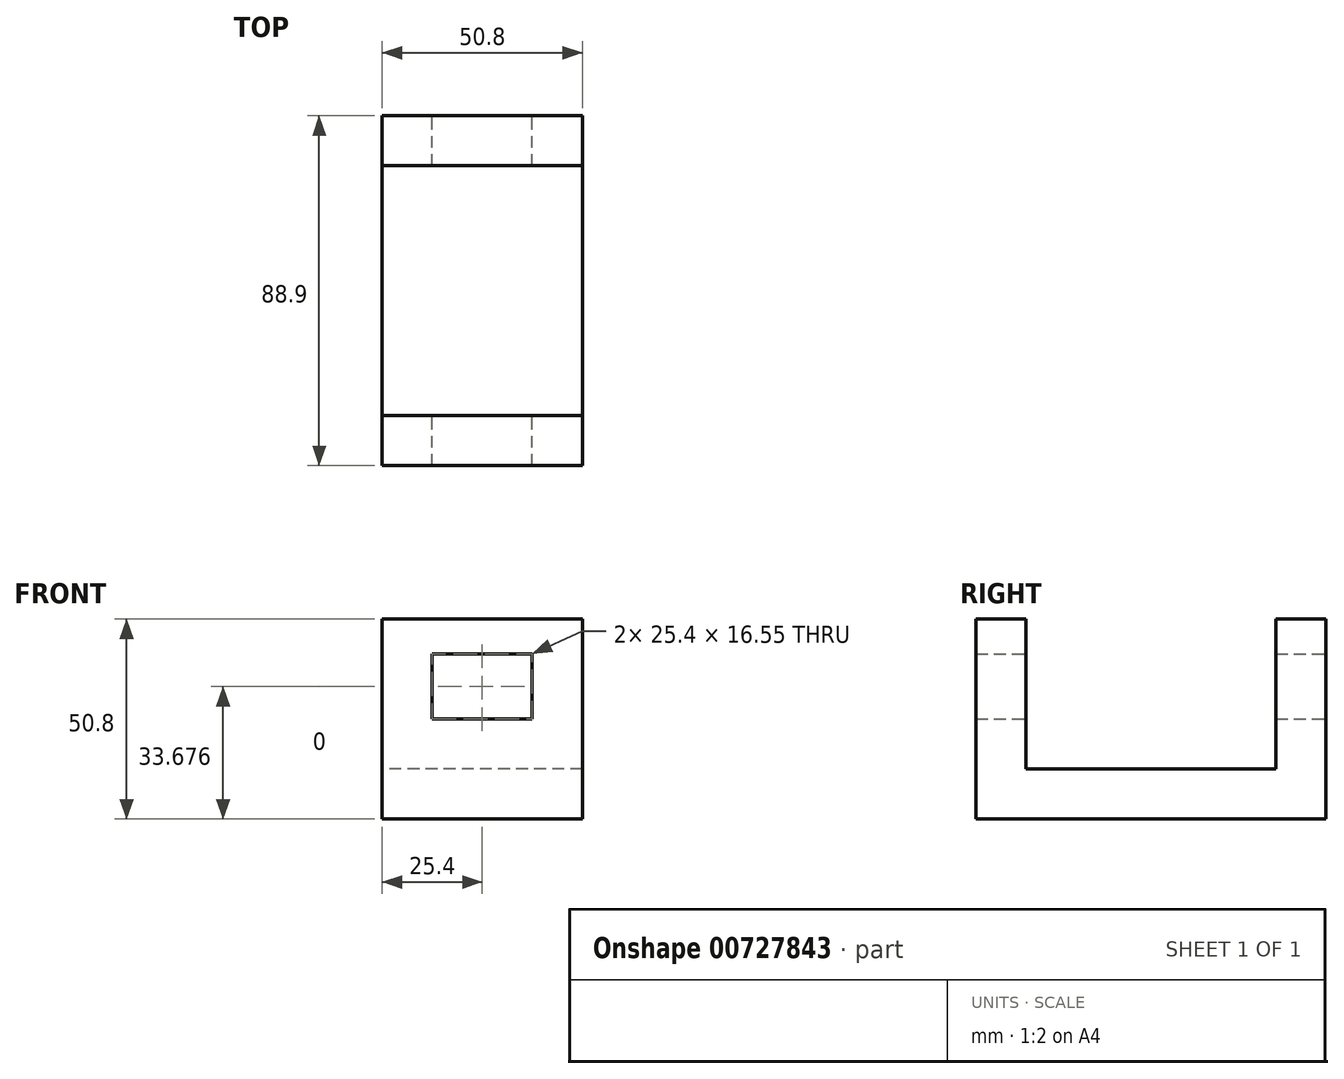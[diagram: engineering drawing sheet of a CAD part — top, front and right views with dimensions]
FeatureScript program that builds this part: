
annotation { "Feature Type Name" : "Feature", "Feature Type Description" : "" }
export const myFeature = defineFeature(function(context is Context, id is Id, definition is map)
    precondition{}
    {
        {
            var Q0;
            Q0=qCreatedBy(makeId("Right.planeOp"),FACE);
            var sketch = newSketch(context, id + "F0", { "sketchPlane" : qUnion([Q0])});
            skLineSegment(sketch, "E0.bottom", {"start": v(44.45, -6.35) * mm, "end": v(-44.45, -6.35) * mm});
            skLineSegment(sketch, "E0.top", {"start": v(44.45, 6.35) * mm, "end": v(-44.45, 6.35) * mm});
            skLineSegment(sketch, "E0.left", {"start": v(44.45, -6.35) * mm, "end": v(44.45, 6.35) * mm});
            skLineSegment(sketch, "E0.right", {"start": v(-44.45, -6.35) * mm, "end": v(-44.45, 6.35) * mm});
            skPoint(sketch, "E0.middle", {"position": v(0, 0) * mm});
            skLineSegment(sketch, "E1.bottom", {"start": v(-44.45, -6.35) * mm, "end": v(-31.75, -6.35) * mm});
            skLineSegment(sketch, "E1.top", {"start": v(-44.45, 44.45) * mm, "end": v(-31.75, 44.45) * mm});
            skLineSegment(sketch, "E1.left", {"start": v(-44.45, -6.35) * mm, "end": v(-44.45, 44.45) * mm});
            skLineSegment(sketch, "E1.right", {"start": v(-31.75, -6.35) * mm, "end": v(-31.75, 44.45) * mm});
            skPoint(sketch, "E2.oppositeSnap0", {"position": v(0, -6.35) * mm});
            skLineSegment(sketch, "E2.bottom", {"start": v(0, 49.89) * mm, "end": v(0, 49.89) * mm});
            skLineSegment(sketch, "E2.top", {"start": v(0, -32.21) * mm, "end": v(0, -32.21) * mm});
            skLineSegment(sketch, "E2.left", {"start": v(0, 49.89) * mm, "end": v(0, -32.21) * mm, "construction": true});
            skLineSegment(sketch, "E2.right", {"start": v(0, 49.89) * mm, "end": v(0, -32.21) * mm, "construction": true});
            skLineSegment(sketch, "E3.MirrorCS", {"start": v(44.45, -6.35) * mm, "end": v(44.45, 44.45) * mm});
            skLineSegment(sketch, "E4.MirrorCS", {"start": v(44.45, 44.45) * mm, "end": v(31.75, 44.45) * mm});
            skLineSegment(sketch, "E5.MirrorCS", {"start": v(31.75, -6.35) * mm, "end": v(31.75, 44.45) * mm});
            skSolve(sketch);
        }
        {
            var Q0;
            Q0 = qSketchRegion(id + "F0", true);
            extrude(context, id + "F1", {"entities" : qUnion([Q0]), "depth" : 50.8 * mm, "offsetDistance" : 25.4 * mm});
        }
        {
            var Q0;
            Q0=makeQuery(id+"F1.opExtrude","SWEPT_FACE",FACE,{"disambiguationData":[OSD([sQuery(id+"F0.wireOp",EDGE,"E3.MirrorCS")])]});
            var sketch = newSketch(context, id + "F2", { "sketchPlane" : qUnion([Q0])});
            skLineSegment(sketch, "E6.bottom", {"start": v(-38.1, 35.6) * mm, "end": v(-12.7, 35.6) * mm});
            skLineSegment(sketch, "E6.top", {"start": v(-38.1, 19.05) * mm, "end": v(-12.7, 19.05) * mm});
            skLineSegment(sketch, "E6.left", {"start": v(-38.1, 35.6) * mm, "end": v(-38.1, 19.05) * mm});
            skLineSegment(sketch, "E6.right", {"start": v(-12.7, 35.6) * mm, "end": v(-12.7, 19.05) * mm});
            skSolve(sketch);
        }
        {
            var Q0;
            Q0=makeQuery(id+"F2.imprint","IMPRINT",FACE,{"disambiguationData":[TD([[makeQuery(id+"F2.imprint","IMPRINT",EDGE,{"derivedFrom":sQuery(id+"F2.wireOp",EDGE,"E6.bottom")}),-1.0]])]});
            extrude(context, id + "F3", {"entities" : qUnion([Q0]), "operationType" : NewBodyOperationType.REMOVE, "oppositeDirection" : true, "depth" : 88.9 * mm, "offsetDistance" : 25.4 * mm});
        }
    });
